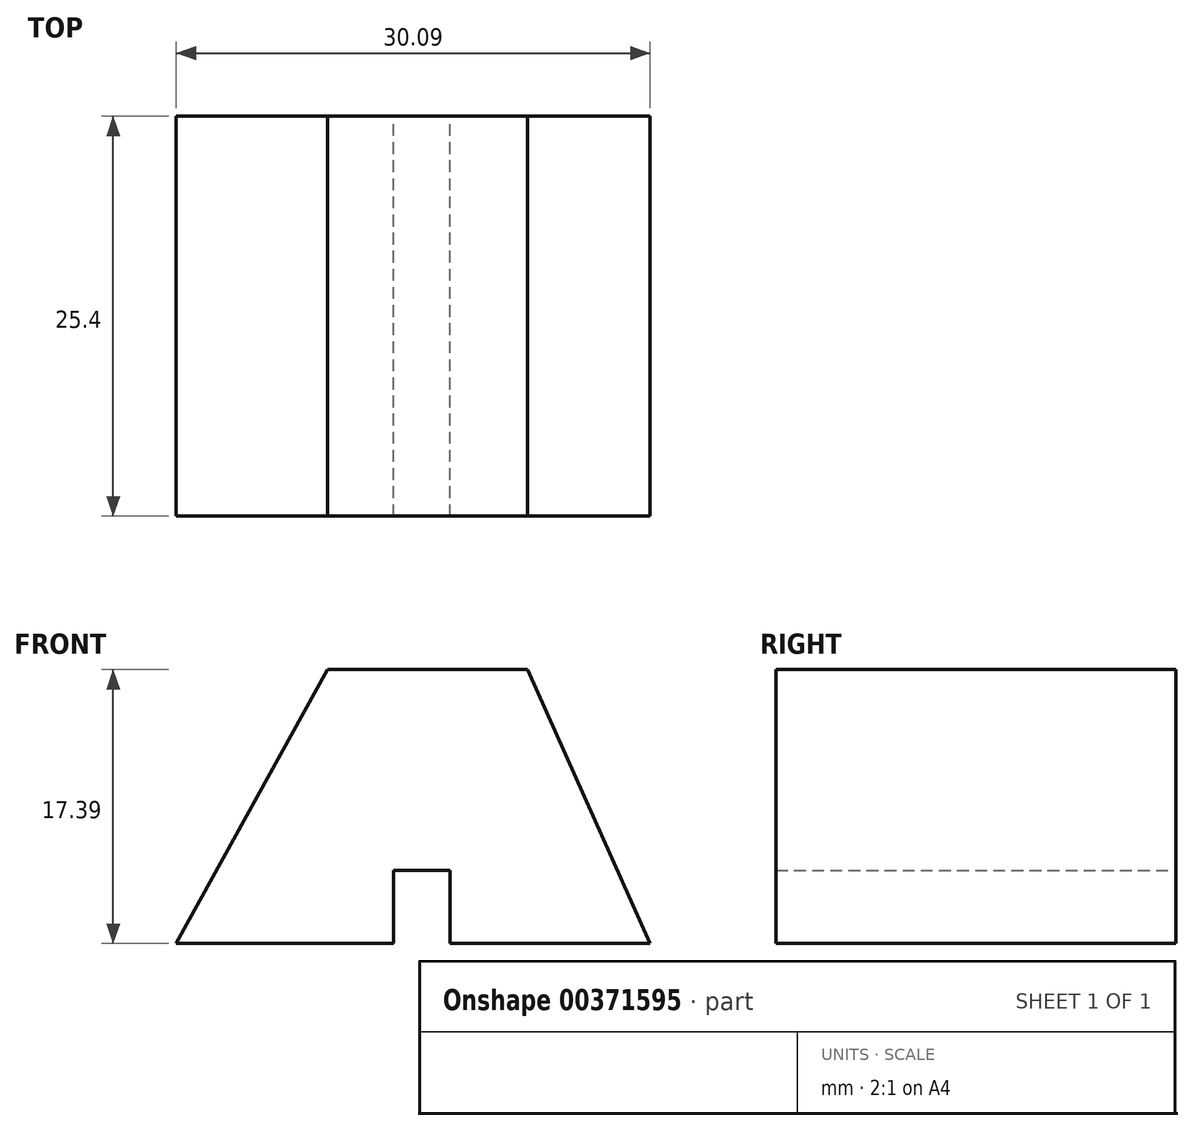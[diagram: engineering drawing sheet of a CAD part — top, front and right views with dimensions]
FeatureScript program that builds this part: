
annotation { "Feature Type Name" : "Feature", "Feature Type Description" : "" }
export const myFeature = defineFeature(function(context is Context, id is Id, definition is map)
    precondition{}
    {
        {
            var Q0;
            Q0=qCreatedBy(makeId("Front.planeOp"),FACE);
            var sketch = newSketch(context, id + "F0", { "sketchPlane" : qUnion([Q0])});
            skLineSegment(sketch, "E0", {"start": v(0, 0) * mm, "end": v(9.6, 17.39) * mm});
            skLineSegment(sketch, "E1", {"start": v(9.6, 17.39) * mm, "end": v(22.3, 17.39) * mm});
            skLineSegment(sketch, "E2", {"start": v(22.3, 17.39) * mm, "end": v(30.1, 0) * mm});
            skLineSegment(sketch, "E3", {"start": v(30.1, 0) * mm, "end": v(17.4, 0) * mm});
            skLineSegment(sketch, "E4", {"start": v(17.4, 0) * mm, "end": v(17.4, 4.62) * mm});
            skLineSegment(sketch, "E5", {"start": v(17.4, 4.62) * mm, "end": v(13.78, 4.62) * mm});
            skLineSegment(sketch, "E6", {"start": v(13.78, 4.62) * mm, "end": v(13.78, 0) * mm});
            skLineSegment(sketch, "E7", {"start": v(13.78, 0) * mm, "end": v(0, 0) * mm});
            skSolve(sketch);
        }
        {
            var Q0;
            Q0 = qSketchRegion(id + "F0", true);
            extrude(context, id + "F1", {"entities" : qUnion([Q0]), "depth" : 25.4 * mm});
        }
    });
